# Revit family: CFLLED_Wall-Hosted_R16_V1.0
name_source: partatom
category: Lighting Fixtures
revit_build: Autodesk Revit 2016 (Build: 20151007_0715(x64)
units: mm (PartAtom-declared; Revit-internal decimal feet)

## family parameters
Always vertical = Yes
Cut with Voids When Loaded = No
Host = Wall
Light Source = Yes
OmniClass Number = 23.80.70.00
OmniClass Title = Lighting
Part Type = Normal
Room Calculation Point = No
Round Connector Dimension = Use Diameter
Shared = No

## types (8) — shared parameters
AS2293 Classification = C0=N/A, C90 = N/A
Battery = 3.2V 6400mAh
Battery type = Lithium Iron Phosphate
Charger Method = Intelligent Current Limited Constant Voltage
Color Filter = 16777215
Dimensions Main Enclosure (L x W x H) = 282mm (W) x 137mm (H) x 64mm (D)
Dimming Lamp Color Temperature Shift = <None>
Emit Shape Visible in Rendering = No
Emit from Rectangle Length = 1219 mm
Emit from Rectangle Width = 610 mm
IP Rating = IP20
Manufacturer = Clevertronics
Mounting = Surface mounted. Supplied with flex and plug. (Flex and plug can be removed)
Operating Mode = Non-maintained
Operating Temperature = 1 - 40C
Operating Voltage = 240V AC; 50Hz
Photometric Web File = ll19124 - CFLLED-ZW.IES
Power Consumption = 2.2W (Max); 0.4W (Standby)
Replacement Driver = 8002390 PCA:LL-Pro L10 Driver 550mA .#CT10142-L5
Tilt Angle = 90.00°
Total Height (including LEDs) = 255mm
Total Lumen Output = 2 x LED Heads (adjustable), 185lm per lamp head
Weight = 1.3Kg

## per-type parameters (varying)
| type | Construction | Inverter/Charger | Model | Other Modules | Product Description | Replacement Battery | Replacement Lamp (Left) | Replacement Lamp (Right) | Testing System |
| CFLLED | Polycarbonate |  | CFLLED LP LED Supalite |  | LP Premium Supalite LED Flood Unit, Surface Mounted Emergency Light, Enabled with Clevertest Plus
LP Premium Supalite LED Flood Unit, Surface | 1550230 BATT:LP 3.2V 6400mAh.200mm lead.Brkt. | 1100954 LED Flood Lamp Head Assy, Cables & Cnnctr, Left | 1100955 LED Flood Lamp Head Assy, Cables & Cnnctr, Right | Clevertest Plus Enabled (Not activated by default) |
| CFLLED-CT | Polycarbonate | Integrated | CFLLD-CT LP LED Supalite (Clevertest) | 8001730 PCA:STU t/s Clever-test, #CT10080-A5 | LP Premium Supalite LED Flood Unit, Surface Mounted Emergency Light
LP Premium Supalite LED Flood Unit, Surface | 1550230 BATT:LP 3.2V 6400mAh.200mm lead.Brkt. | 1100954 LED Flood Lamp Head Assy, Cables & Cnnctr,Left | 1100955 LED Flood Lamp Head Assy, Cables & Cnnctr,Right | Clevertest |
| CFLLED-DALI | Polycarbonate |  | CFLLED-DALI LP LED Supalite (DALI) | 8002200 PCA:DALI Node, #CT10410-A3 | LP Premium Supalite LED Flood Unit, Surface Mounted Emergency Light | 1550230 BATT:LP 3.2V 6400mAh.200mm lead.Brkt. | 1100954 LED Flood Lamp Head Assy, Cables & Cnnctr,Left | 1100955 LED Flood Lamp Head Assy, Cables & Cnnctr,Right | DALI compatible |
| CFLLED-ZW | Polycarbonate |  | CFLLED-ZW LP LED Supalite (Zoneworks) | 8001450 PCA:Powerline Node ZW, #CT10310-A6 | LP Premium Supalite LED Flood Unit, Surface Mounted Emergency Light | 1550230 BATT:LP 3.2V 6400mAh.200mm lead.Brkt. | 1100954 LED Flood Lamp Head Assy, Cables & Cnnctr,Left | 1100955 LED Flood Lamp Head Assy, Cables & Cnnctr,Right | Zoneworks computerised testing |
| CFLLED-ZW-4HR | Polycarbonate |  | CFLLED-ZW-4HR LP LED Supalite with 4hr duration (Zoneworks) | 8001450 PCA:Powerline Node ZW, #CT10310-A6 | LP Premium LED Supalite Flood Unit, surface mount, emergency light – 4 hour duration | 1550230 BATT:LP 3.2V 6400mAh.200mm lead.Brkt. (2) | 1100954 LED Flood Lamp Head Assy, Cables & Cnnctr,Left | 1100955 LED Flood Lamp Head Assy, Cables & Cnnctr,Right | Zoneworks computerised testing |
| CFLLED-BLK | Polycarbonate, Black |  | CFLLED-BLK LP LED Supalite Black |  | LP Premium Supalite LED Flood Unit, Surface Mounted Emergency Light, Black | 1550230 BATT:LP 3.2V 6400mAh.200mm lead.Brkt. | 1100956 LED Flood LampHead Ass,Cable&Ctr,LeftBLK | 1100957 LED Flood LampHeadAss,Cable&Ctr,RightBLK | Manual Test Switch |
| CFLLED-DALI-BLK | Polycarbonate, Black |  | CFLLED-DALI-BLK LP LED Supalite | 8003060 PCA: DALI Node #CT10629-Ax | LP Premium Supalite LED Flood Unit, Surface Mounted Emergency Light, Black | 1550230 BATT:LP 3.2V 6400mAh.200mm lead.Brkt. | 1100956 LED Flood LampHead Ass,Cable&Ctr,LeftBLK | 1100957 LED Flood LampHeadAss,Cable&Ctr,RightBLK | DALI Compatible |
| CFLLED-ZW-BLK | Polycarbonate, Black |  | CFLLED-ZW-BLK LP LED Supalite (Zoneworks) | 8001450 PCA:Powerline Node ZW, #CT10310-A6 | LP Premium Supalite LED Flood Unit, Surface Mounted Emergency Light, Black | 1550230 BATT:LP 3.2V 6400mAh.200mm lead.Brkt. | 1100956 LED Flood LampHead Ass,Cable&Ctr,LeftBLK | 1100957 LED Flood LampHeadAss,Cable&Ctr,RightBLK | Zoneworks computerised testing |

## geometry (parser evidence)
native form markers: Blend x4, Sweep x3
no freeform markers — native parametric forms only
